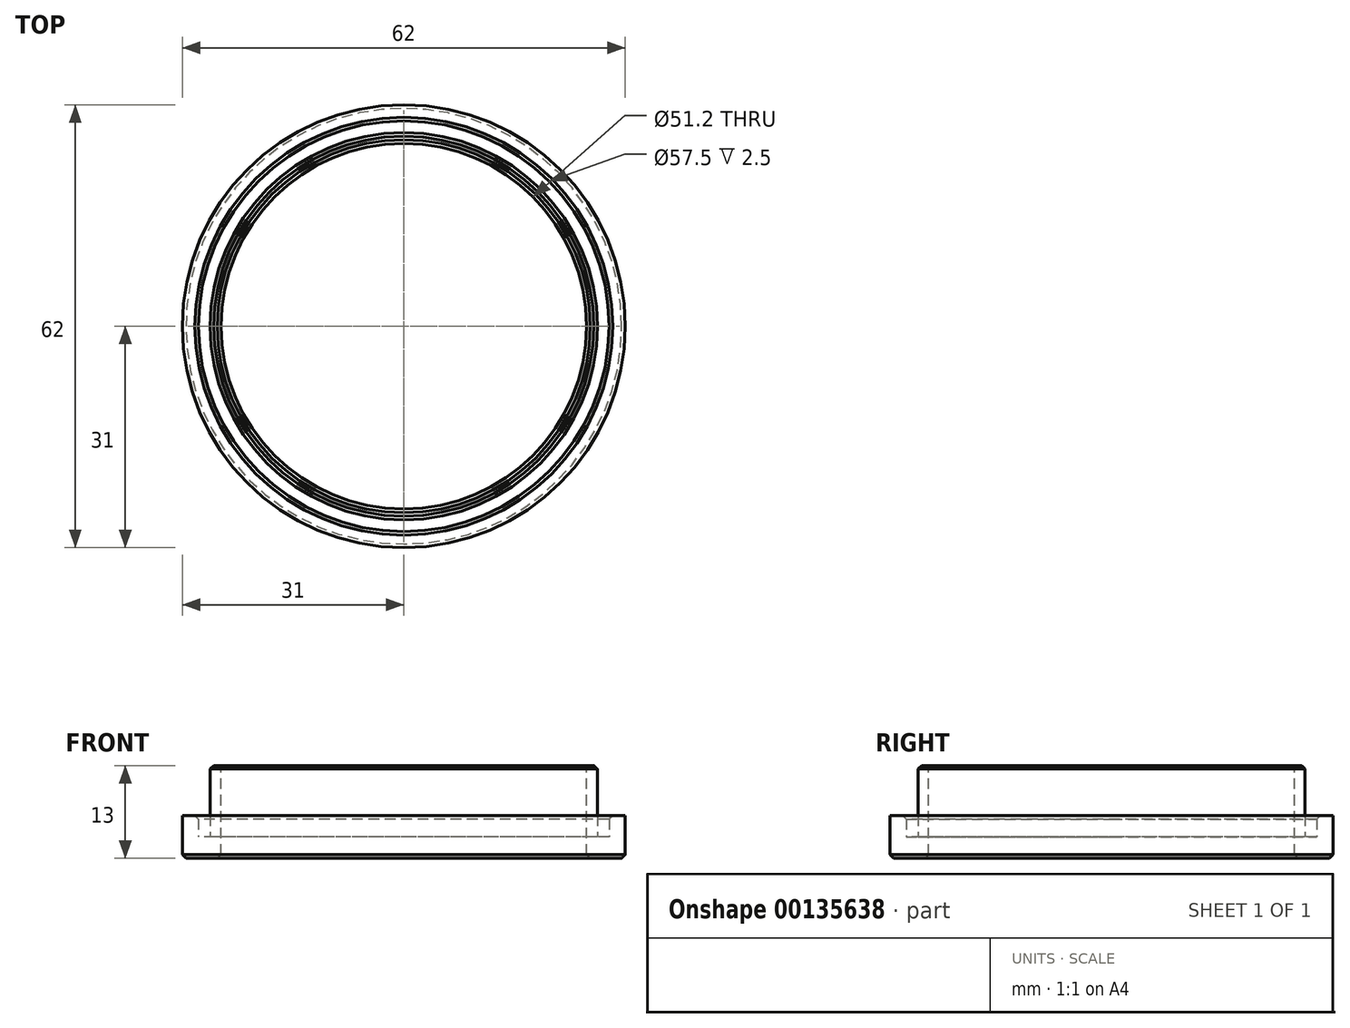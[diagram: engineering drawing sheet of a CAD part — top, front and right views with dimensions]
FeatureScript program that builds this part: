
annotation { "Feature Type Name" : "Feature", "Feature Type Description" : "" }
export const myFeature = defineFeature(function(context is Context, id is Id, definition is map)
    precondition{}
    {
        {
            var Q0;
            Q0=qCreatedBy(makeId("Top.planeOp"),FACE);
            var sketch = newSketch(context, id + "F0", { "sketchPlane" : qUnion([Q0])});
            skCircle(sketch, "E0", {"center": v(0, 0) * mm, "radius": 31 * mm});
            skCircle(sketch, "E1", {"center": v(0, 0) * mm, "radius": 27.1 * mm});
            skCircle(sketch, "E2", {"center": v(0, 0) * mm, "radius": 25.6 * mm});
            skCircle(sketch, "E3", {"center": v(0, 0) * mm, "radius": 28.75 * mm});
            skSolve(sketch);
        }
        {
            var Q0;
            Q0=makeQuery(id+"F0.imprint","IMPRINT",FACE,{"disambiguationData":[TD([[makeQuery(id+"F0.imprint","IMPRINT",EDGE,{"derivedFrom":sQuery(id+"F0.wireOp",EDGE,"E1")}),1.0]])]});
            var Q1;
            Q1=makeQuery(id+"F0.imprint","IMPRINT",FACE,{"disambiguationData":[TD([[makeQuery(id+"F0.imprint","IMPRINT",EDGE,{"derivedFrom":sQuery(id+"F0.wireOp",EDGE,"E1")}),-1.0]])]});
            var Q2;
            Q2=makeQuery(id+"F0.imprint","IMPRINT",FACE,{"disambiguationData":[TD([[makeQuery(id+"F0.imprint","IMPRINT",EDGE,{"derivedFrom":sQuery(id+"F0.wireOp",EDGE,"E0")}),1.0]])]});
            extrude(context, id + "F1", {"entities" : qUnion([Q0, Q1, Q2]), "oppositeDirection" : true, "depth" : 3 * mm});
        }
        {
            var Q0;
            Q0=makeQuery(id+"F0.imprint","IMPRINT",FACE,{"disambiguationData":[TD([[makeQuery(id+"F0.imprint","IMPRINT",EDGE,{"derivedFrom":sQuery(id+"F0.wireOp",EDGE,"E1")}),1.0]])]});
            extrude(context, id + "F2", {"entities" : qUnion([Q0]), "operationType" : NewBodyOperationType.ADD, "depth" : 10 * mm});
        }
        {
            var Q0;
            Q0=makeQuery(id+"F0.imprint","IMPRINT",FACE,{"disambiguationData":[TD([[makeQuery(id+"F0.imprint","IMPRINT",EDGE,{"derivedFrom":sQuery(id+"F0.wireOp",EDGE,"E0")}),1.0]])]});
            extrude(context, id + "F3", {"entities" : qUnion([Q0]), "operationType" : NewBodyOperationType.ADD, "depth" : 3 * mm});
        }
        {
            var Q0;
            Q0=makeQuery(id+"F0.imprint","IMPRINT",FACE,{"disambiguationData":[TD([[makeQuery(id+"F0.imprint","IMPRINT",EDGE,{"derivedFrom":sQuery(id+"F0.wireOp",EDGE,"E2")}),1.0]])]});
            extrude(context, id + "F4", {"entities" : qUnion([Q0]), "operationType" : NewBodyOperationType.REMOVE, "depth" : 25 * mm});
        }
        {
            var Q0;
            Q0=makeQuery(id+"F2.opExtrude","CAP_EDGE",EDGE,{"disambiguationData":[OSD([sQuery(id+"F0.wireOp",EDGE,"E2")])],"isStart":false});
            var Q1;
            Q1=makeQuery(id+"F2.opExtrude","CAP_EDGE",EDGE,{"disambiguationData":[OSD([sQuery(id+"F0.wireOp",EDGE,"E1")])],"isStart":false});
            var Q2;
            Q2=makeQuery(id+"F3.opExtrude","CAP_EDGE",EDGE,{"disambiguationData":[OSD([sQuery(id+"F0.wireOp",EDGE,"E3")])],"isStart":false});
            var Q3;
            Q3=makeQuery(id+"F1.opExtrude","CAP_EDGE",EDGE,{"disambiguationData":[OSD([sQuery(id+"F0.wireOp",EDGE,"E2")])],"isStart":false});
            var Q4;
            Q4=makeQuery(id+"F1.opExtrude","CAP_EDGE",EDGE,{"disambiguationData":[OSD([sQuery(id+"F0.wireOp",EDGE,"E0")])],"isStart":false});
            chamfer(context, id + "F5", {"entities" : qUnion([Q0, Q1, Q2, Q3, Q4]), "width" : 0.5 * mm, "tangentPropagation" : true});
        }
    });
